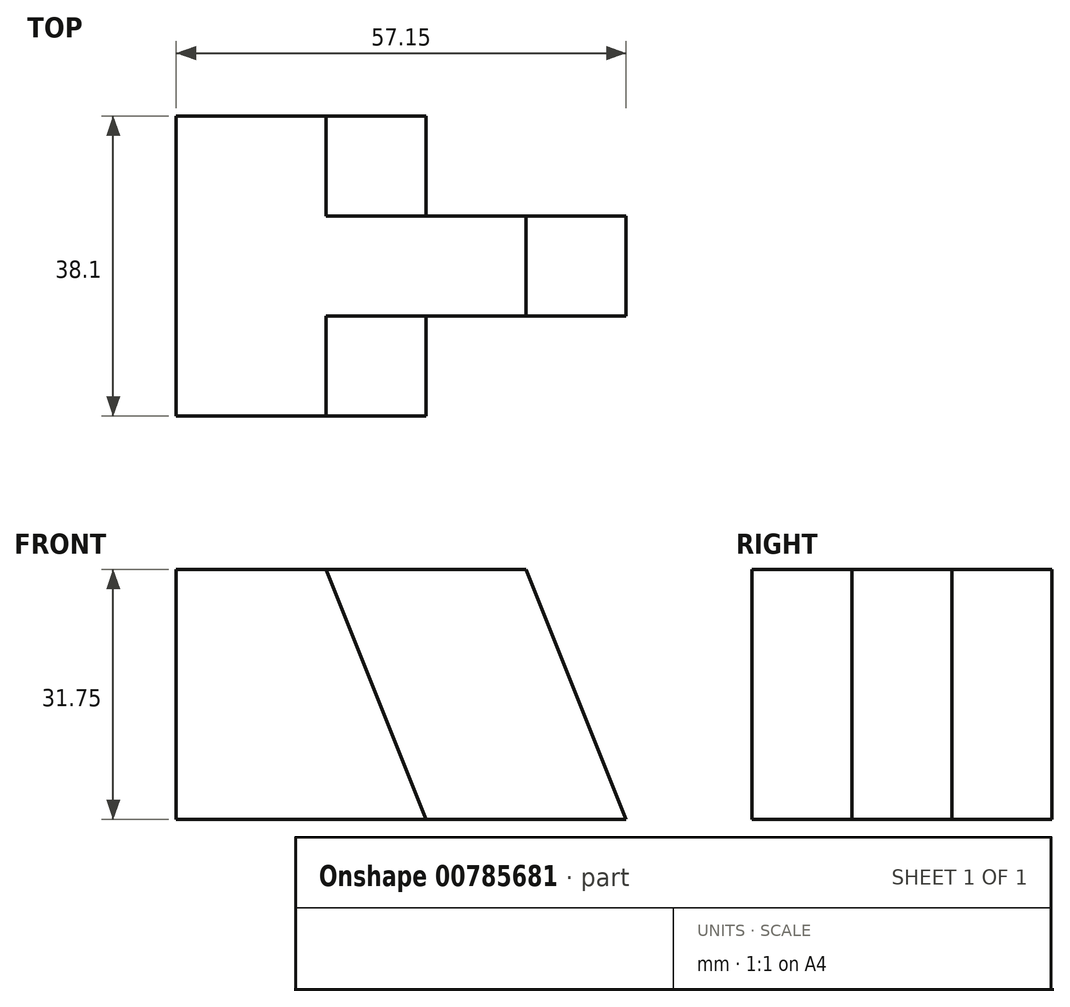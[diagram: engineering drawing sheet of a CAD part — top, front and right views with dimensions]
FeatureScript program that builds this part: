
annotation { "Feature Type Name" : "Feature", "Feature Type Description" : "" }
export const myFeature = defineFeature(function(context is Context, id is Id, definition is map)
    precondition{}
    {
        {
            var Q0;
            Q0=qCreatedBy(makeId("Front.planeOp"),FACE);
            var sketch = newSketch(context, id + "F0", { "sketchPlane" : qUnion([Q0])});
            skLineSegment(sketch, "E0", {"start": v(0, 0) * mm, "end": v(57.15, 0) * mm});
            skLineSegment(sketch, "E1", {"start": v(57.15, 0) * mm, "end": v(57.15, 31.75) * mm});
            skLineSegment(sketch, "E2", {"start": v(57.15, 31.75) * mm, "end": v(0, 31.75) * mm});
            skLineSegment(sketch, "E3", {"start": v(0, 31.75) * mm, "end": v(0, 0) * mm});
            skSolve(sketch);
        }
        {
            var Q0;
            Q0=makeQuery(id+"F0.imprint","IMPRINT",FACE,{"disambiguationData":[TD([[makeQuery(id+"F0.imprint","IMPRINT",EDGE,{"derivedFrom":sQuery(id+"F0.wireOp",EDGE,"E0")}),1.0]])]});
            extrude(context, id + "F1", {"entities" : qUnion([Q0]), "oppositeDirection" : true, "depth" : 38.1 * mm, "offsetDistance" : 25.4 * mm});
        }
        {
            var Q0;
            Q0=makeQuery(id+"F1.opExtrude","CAP_FACE",FACE,{"disambiguationData":[OSD([sQuery(id+"F0.wireOp",EDGE,"E0"),sQuery(id+"F0.wireOp",EDGE,"E1"),sQuery(id+"F0.wireOp",EDGE,"E2"),sQuery(id+"F0.wireOp",EDGE,"E3")])],"isStart":true});
            var sketch = newSketch(context, id + "F2", { "sketchPlane" : qUnion([Q0])});
            skLineSegment(sketch, "E4", {"start": v(0, 31.75) * mm, "end": v(44.45, 31.75) * mm});
            skLineSegment(sketch, "E5", {"start": v(44.45, 31.75) * mm, "end": v(57.15, 0) * mm});
            skSolve(sketch);
        }
        {
            var Q0;
            Q0 = qSketchRegion(id + "F2", true);
            var Q1;
            {var subQ0=sQuery(id+"F2.wireOp",EDGE,"E5");Q1=makeQuery(id+"F2.imprint","IMPRINT",FACE,{"disambiguationData":[TD([[makeQuery(id+"F2.imprint","IMPRINT",EDGE,{"derivedFrom":subQ0}),1.0]])]});}
            extrude(context, id + "F3", {"entities" : qUnion([Q0, Q1]), "operationType" : NewBodyOperationType.REMOVE, "oppositeDirection" : true, "depth" : 38.1 * mm, "offsetDistance" : 25.4 * mm});
        }
        {
            var Q0;
            Q0=makeQuery(id+"F1.opExtrude","CAP_FACE",FACE,{"disambiguationData":[OSD([sQuery(id+"F0.wireOp",EDGE,"E0"),sQuery(id+"F0.wireOp",EDGE,"E1"),sQuery(id+"F0.wireOp",EDGE,"E2"),sQuery(id+"F0.wireOp",EDGE,"E3")])],"isStart":true});
            var sketch = newSketch(context, id + "F4", { "sketchPlane" : qUnion([Q0])});
            skLineSegment(sketch, "E6", {"start": v(0, 0) * mm, "end": v(31.75, 0) * mm});
            skLineSegment(sketch, "E7", {"start": v(0, 31.75) * mm, "end": v(19.05, 31.75) * mm});
            skLineSegment(sketch, "E8", {"start": v(19.05, 31.75) * mm, "end": v(31.75, 0) * mm});
            skLineSegment(sketch, "E9", {"start": v(0, 0) * mm, "end": v(0, 31.75) * mm});
            skSolve(sketch);
        }
        {
            var Q0;
            {var subQ0=sQuery(id+"F4.wireOp",EDGE,"E8");Q0=makeQuery(id+"F4.imprint","IMPRINT",FACE,{"disambiguationData":[TD([[makeQuery(id+"F4.imprint","IMPRINT",EDGE,{"derivedFrom":subQ0}),1.0]])]});}
            extrude(context, id + "F5", {"entities" : qUnion([Q0]), "operationType" : NewBodyOperationType.REMOVE, "oppositeDirection" : true, "depth" : 12.7 * mm, "offsetDistance" : 25.4 * mm});
        }
        {
            var Q0;
            Q0=makeQuery(id+"F1.opExtrude","CAP_FACE",FACE,{"disambiguationData":[OSD([sQuery(id+"F0.wireOp",EDGE,"E0"),sQuery(id+"F0.wireOp",EDGE,"E1"),sQuery(id+"F0.wireOp",EDGE,"E2"),sQuery(id+"F0.wireOp",EDGE,"E3")])],"isStart":false});
            var sketch = newSketch(context, id + "F6", { "sketchPlane" : qUnion([Q0])});
            skLineSegment(sketch, "E10", {"start": v(0, 0) * mm, "end": v(-31.75, 0) * mm});
            skLineSegment(sketch, "E11", {"start": v(0, 31.75) * mm, "end": v(-19.05, 31.75) * mm});
            skLineSegment(sketch, "E12", {"start": v(-19.05, 31.75) * mm, "end": v(-31.75, 0) * mm});
            skSolve(sketch);
        }
        {
            var Q0;
            {var subQ0=sQuery(id+"F6.wireOp",EDGE,"E12");Q0=makeQuery(id+"F6.imprint","IMPRINT",FACE,{"disambiguationData":[TD([[makeQuery(id+"F6.imprint","IMPRINT",EDGE,{"derivedFrom":subQ0}),-1.0]])]});}
            extrude(context, id + "F7", {"entities" : qUnion([Q0]), "operationType" : NewBodyOperationType.REMOVE, "oppositeDirection" : true, "depth" : 12.7 * mm, "offsetDistance" : 25.4 * mm});
        }
    });
